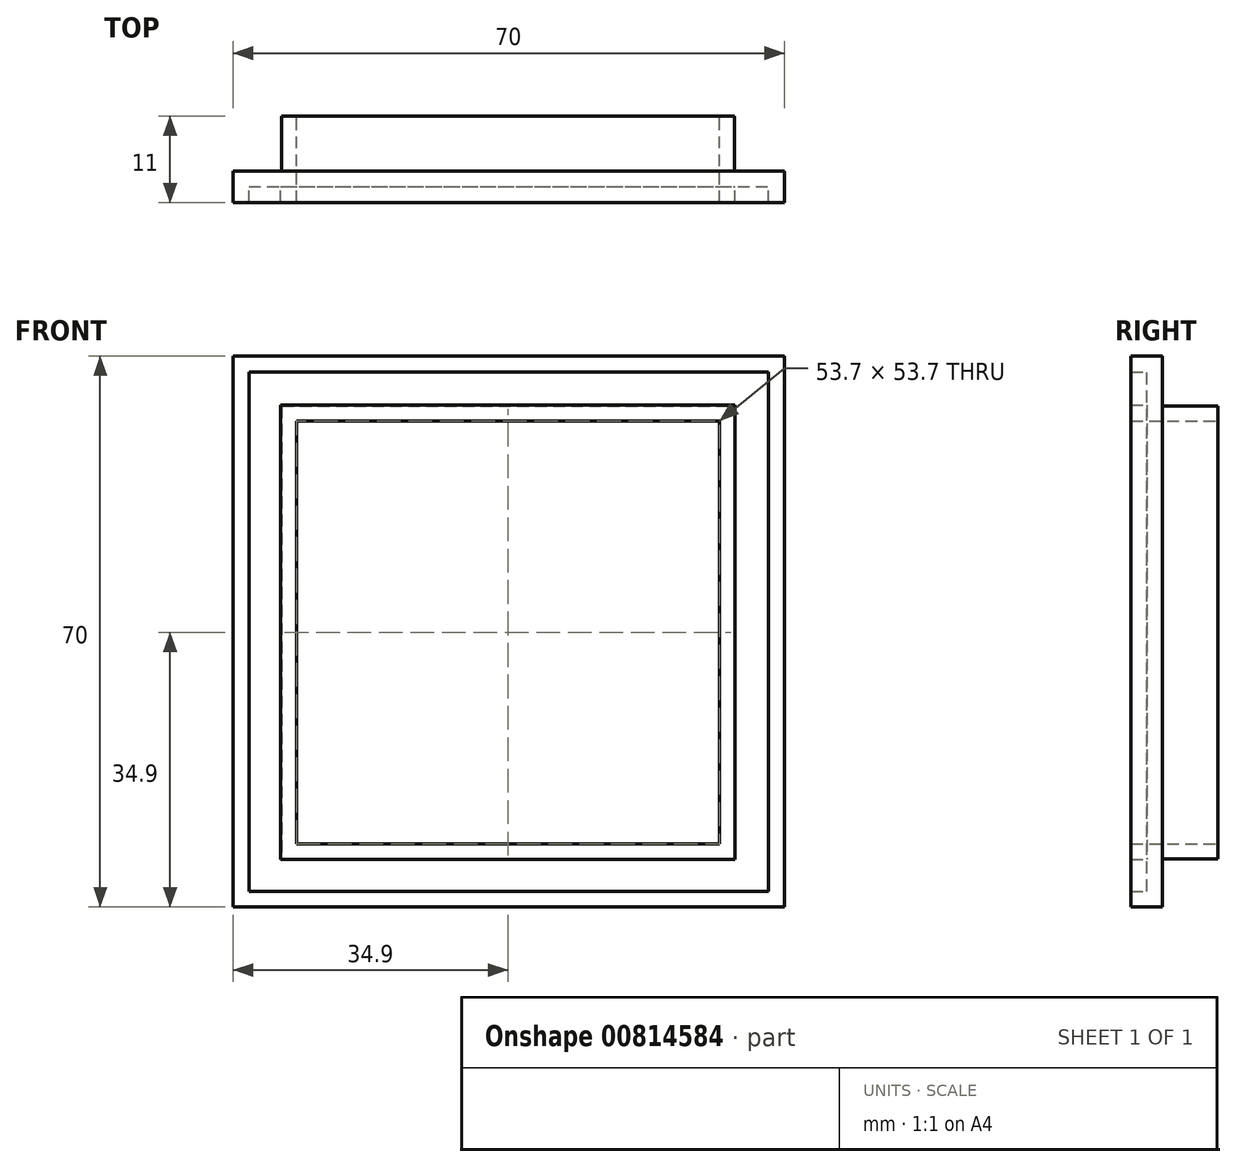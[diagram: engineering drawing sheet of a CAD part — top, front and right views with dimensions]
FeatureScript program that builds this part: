
annotation { "Feature Type Name" : "Feature", "Feature Type Description" : "" }
export const myFeature = defineFeature(function(context is Context, id is Id, definition is map)
    precondition{}
    {
        {
            var Q0;
            Q0=qCreatedBy(makeId("Front.planeOp"),FACE);
            var sketch = newSketch(context, id + "F0", { "sketchPlane" : qUnion([Q0])});
            skLineSegment(sketch, "E0.bottom", {"start": v(0, 0) * mm, "end": v(70, 0) * mm});
            skLineSegment(sketch, "E0.top", {"start": v(0, 70) * mm, "end": v(70, 70) * mm});
            skLineSegment(sketch, "E0.left", {"start": v(0, 0) * mm, "end": v(0, 70) * mm});
            skLineSegment(sketch, "E0.right", {"start": v(70, 0) * mm, "end": v(70, 70) * mm});
            skLineSegment(sketch, "E1.bottom", {"start": v(2.75, 67.25) * mm, "end": v(67.25, 67.25) * mm});
            skLineSegment(sketch, "E1.top", {"start": v(2.75, 2.75) * mm, "end": v(67.25, 2.75) * mm});
            skLineSegment(sketch, "E1.left", {"start": v(2.75, 67.25) * mm, "end": v(2.75, 2.75) * mm});
            skLineSegment(sketch, "E1.right", {"start": v(67.25, 67.25) * mm, "end": v(67.25, 2.75) * mm});
            skLineSegment(sketch, "E2.bottom", {"start": v(8.05, 61.75) * mm, "end": v(61.75, 61.75) * mm});
            skLineSegment(sketch, "E2.top", {"start": v(8.05, 8.05) * mm, "end": v(61.75, 8.05) * mm});
            skLineSegment(sketch, "E2.left", {"start": v(8.05, 61.75) * mm, "end": v(8.05, 8.05) * mm});
            skLineSegment(sketch, "E2.right", {"start": v(61.75, 61.75) * mm, "end": v(61.75, 8.05) * mm});
            skLineSegment(sketch, "E3.bottom", {"start": v(6.15, 63.65) * mm, "end": v(63.65, 63.65) * mm});
            skLineSegment(sketch, "E3.top", {"start": v(6.15, 6.15) * mm, "end": v(63.65, 6.15) * mm});
            skLineSegment(sketch, "E3.left", {"start": v(6.15, 63.65) * mm, "end": v(6.15, 6.15) * mm});
            skLineSegment(sketch, "E3.right", {"start": v(63.65, 63.65) * mm, "end": v(63.65, 6.15) * mm});
            skSolve(sketch);
        }
        {
            var Q0;
            Q0=makeQuery(id+"F0.imprint","IMPRINT",FACE,{"disambiguationData":[TD([[makeQuery(id+"F0.imprint","IMPRINT",EDGE,{"derivedFrom":sQuery(id+"F0.wireOp",EDGE,"E0.bottom")}),1.0]])]});
            var Q1;
            Q1=makeQuery(id+"F0.imprint","IMPRINT",FACE,{"disambiguationData":[TD([[makeQuery(id+"F0.imprint","IMPRINT",EDGE,{"derivedFrom":sQuery(id+"F0.wireOp",EDGE,"E1.bottom")}),-1.0]])]});
            var Q2;
            Q2=makeQuery(id+"F0.imprint","IMPRINT",FACE,{"disambiguationData":[TD([[makeQuery(id+"F0.imprint","IMPRINT",EDGE,{"derivedFrom":sQuery(id+"F0.wireOp",EDGE,"E2.bottom")}),1.0]])]});
            extrude(context, id + "F1", {"entities" : qUnion([Q0, Q1, Q2]), "depth" : 11 * mm, "offsetDistance" : 25 * mm});
        }
        {
            var Q0;
            Q0 = qSketchRegion(id + "F0", true);
            var Q1;
            Q1=makeQuery(id+"F0.imprint","IMPRINT",FACE,{"disambiguationData":[TD([[makeQuery(id+"F0.imprint","IMPRINT",EDGE,{"derivedFrom":sQuery(id+"F0.wireOp",EDGE,"E1.bottom")}),-1.0]])]});
            extrude(context, id + "F2", {"entities" : qUnion([Q0, Q1]), "operationType" : NewBodyOperationType.REMOVE, "depth" : 7 * mm, "offsetDistance" : 25 * mm});
        }
        {
            var Q0;
            Q0=makeQuery(id+"F1.opExtrude","CAP_FACE",FACE,{"disambiguationData":[OSD([sQuery(id+"F0.wireOp",EDGE,"E0.bottom"),sQuery(id+"F0.wireOp",EDGE,"E0.top"),sQuery(id+"F0.wireOp",EDGE,"E0.left"),sQuery(id+"F0.wireOp",EDGE,"E0.right"),sQuery(id+"F0.wireOp",EDGE,"E2.bottom"),sQuery(id+"F0.wireOp",EDGE,"E2.top"),sQuery(id+"F0.wireOp",EDGE,"E2.left"),sQuery(id+"F0.wireOp",EDGE,"E2.right")])],"isStart":false});
            shell(context, id + "F3", {"entities" : qUnion([Q0]), "thickness" : 2 * mm});
        }
    });
